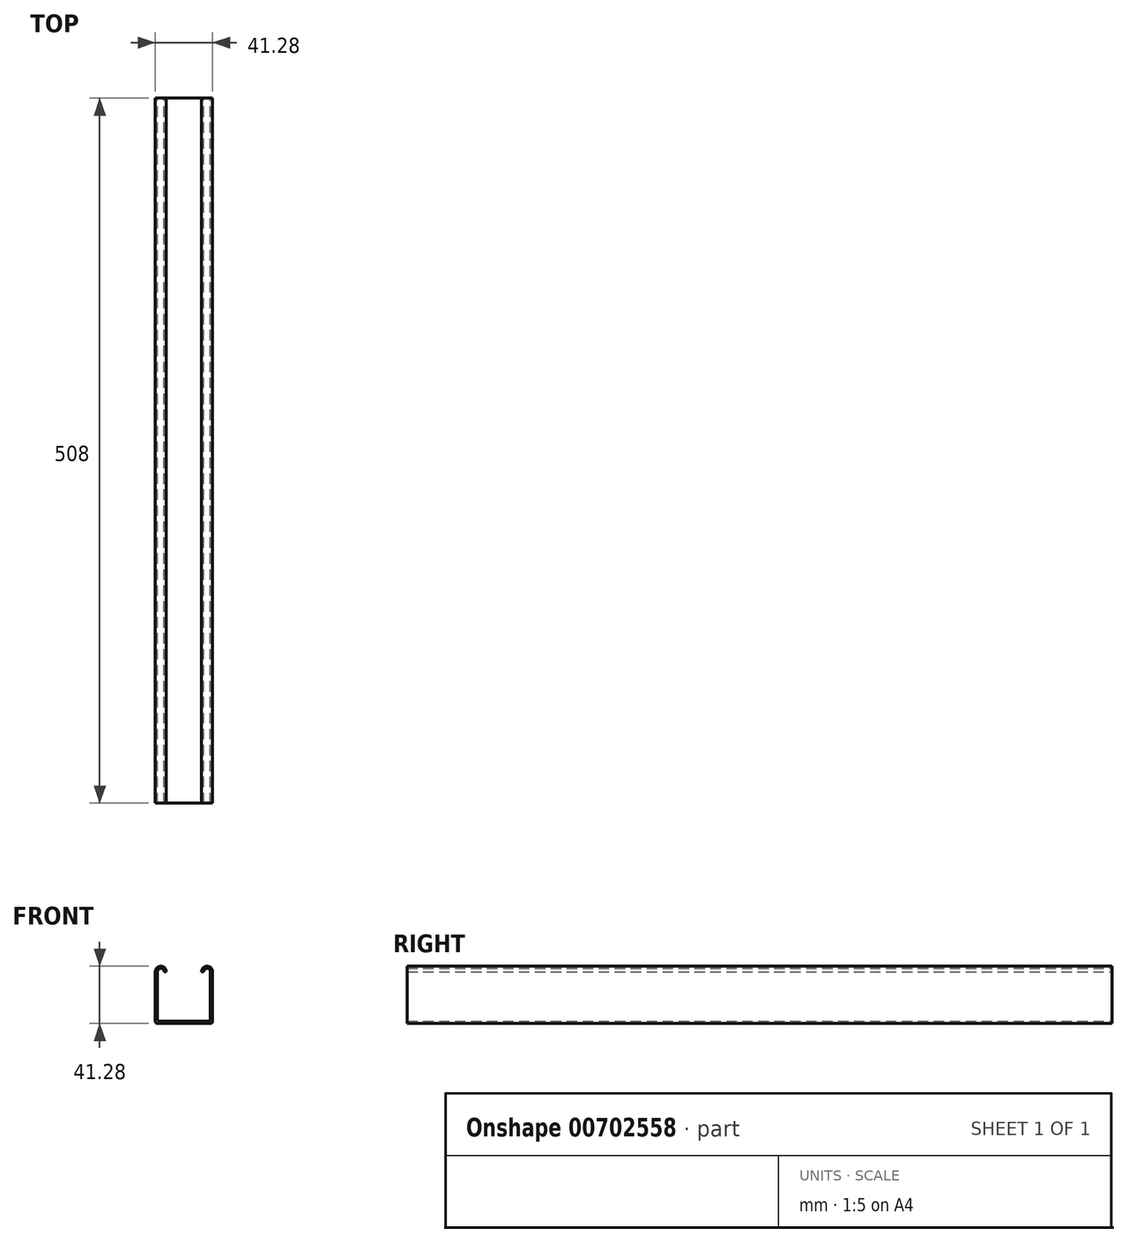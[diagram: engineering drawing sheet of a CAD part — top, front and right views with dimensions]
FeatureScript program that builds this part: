
annotation { "Feature Type Name" : "Feature", "Feature Type Description" : "" }
export const myFeature = defineFeature(function(context is Context, id is Id, definition is map)
    precondition{}
    {
        {
            var Q0;
            Q0=qCreatedBy(makeId("Front.planeOp"),FACE);
            var sketch = newSketch(context, id + "F0", { "sketchPlane" : qUnion([Q0])});
            skLineSegment(sketch, "E0.bottom", {"start": v(20.64, -20.64) * mm, "end": v(-20.64, -20.64) * mm});
            skLineSegment(sketch, "E0.left", {"start": v(20.64, -20.64) * mm, "end": v(20.64, 16.67) * mm});
            skLineSegment(sketch, "E0.right", {"start": v(-20.64, -20.64) * mm, "end": v(-20.64, 16.67) * mm});
            skPoint(sketch, "E0.middle", {"position": v(0, 0) * mm});
            skLineSegment(sketch, "E1.0", {"start": v(-19.05, -19.05) * mm, "end": v(-19.05, 16.67) * mm});
            skLineSegment(sketch, "E2.0", {"start": v(19.05, -19.05) * mm, "end": v(-19.05, -19.05) * mm});
            skLineSegment(sketch, "E3.0", {"start": v(19.05, -19.05) * mm, "end": v(19.05, 16.67) * mm});
            skArc(sketch, "E4", {"start": v(-12.7, 16.67) * mm, "mid": v(-16.67, 20.64) * mm, "end": v(-20.64, 16.67) * mm});
            skArc(sketch, "E5", {"start": v(-14.29, 16.67) * mm, "mid": v(-16.67, 19.05) * mm, "end": v(-19.05, 16.67) * mm});
            skLineSegment(sketch, "E6", {"start": v(-12.7, 16.67) * mm, "end": v(-14.29, 16.67) * mm});
            skPoint(sketch, "E7.orphan", {"position": v(-20.64, 20.64) * mm});
            skArc(sketch, "E8.MirrorCS", {"start": v(12.7, 16.67) * mm, "mid": v(16.67, 20.64) * mm, "end": v(20.64, 16.67) * mm});
            skLineSegment(sketch, "E9.MirrorCS", {"start": v(12.7, 16.67) * mm, "end": v(14.29, 16.67) * mm});
            skArc(sketch, "E10.MirrorCS", {"start": v(14.29, 16.67) * mm, "mid": v(16.67, 19.05) * mm, "end": v(19.05, 16.67) * mm});
            skPoint(sketch, "E0.top.start.orphan", {"position": v(20.64, 20.64) * mm});
            skSolve(sketch);
        }
        {
            var Q0;
            Q0 = qSketchRegion(id + "F0", true);
            extrude(context, id + "F1", {"entities" : qUnion([Q0]), "endBound" : BoundingType.SYMMETRIC, "depth" : 508 * mm, "offsetDistance" : 25.4 * mm});
        }
        {
            var Q0;
            Q0=makeQuery(id+"F1.opExtrude","SWEPT_EDGE",EDGE,{"disambiguationData":[OSD([sQuery(id+"F0.wireOp",EDGE,"E1.0"),sQuery(id+"F0.wireOp",EDGE,"E2.0")])]});
            var Q1;
            Q1=makeQuery(id+"F1.opExtrude","SWEPT_EDGE",EDGE,{"disambiguationData":[OSD([sQuery(id+"F0.wireOp",EDGE,"E2.0"),sQuery(id+"F0.wireOp",EDGE,"E3.0")])]});
            var Q2;
            Q2=makeQuery(id+"F1.opExtrude","SWEPT_EDGE",EDGE,{"disambiguationData":[OSD([sQuery(id+"F0.wireOp",EDGE,"E0.bottom"),sQuery(id+"F0.wireOp",EDGE,"E0.left")])]});
            var Q3;
            Q3=makeQuery(id+"F1.opExtrude","SWEPT_EDGE",EDGE,{"disambiguationData":[OSD([sQuery(id+"F0.wireOp",EDGE,"E0.bottom"),sQuery(id+"F0.wireOp",EDGE,"E0.right")])]});
            fillet(context, id + "F2", {"entities" : qUnion([Q0, Q1, Q2, Q3]), "radius" : 1.59 * mm, "tangentPropagation" : true, "allowEdgeOverflow" : false});
        }
    });
